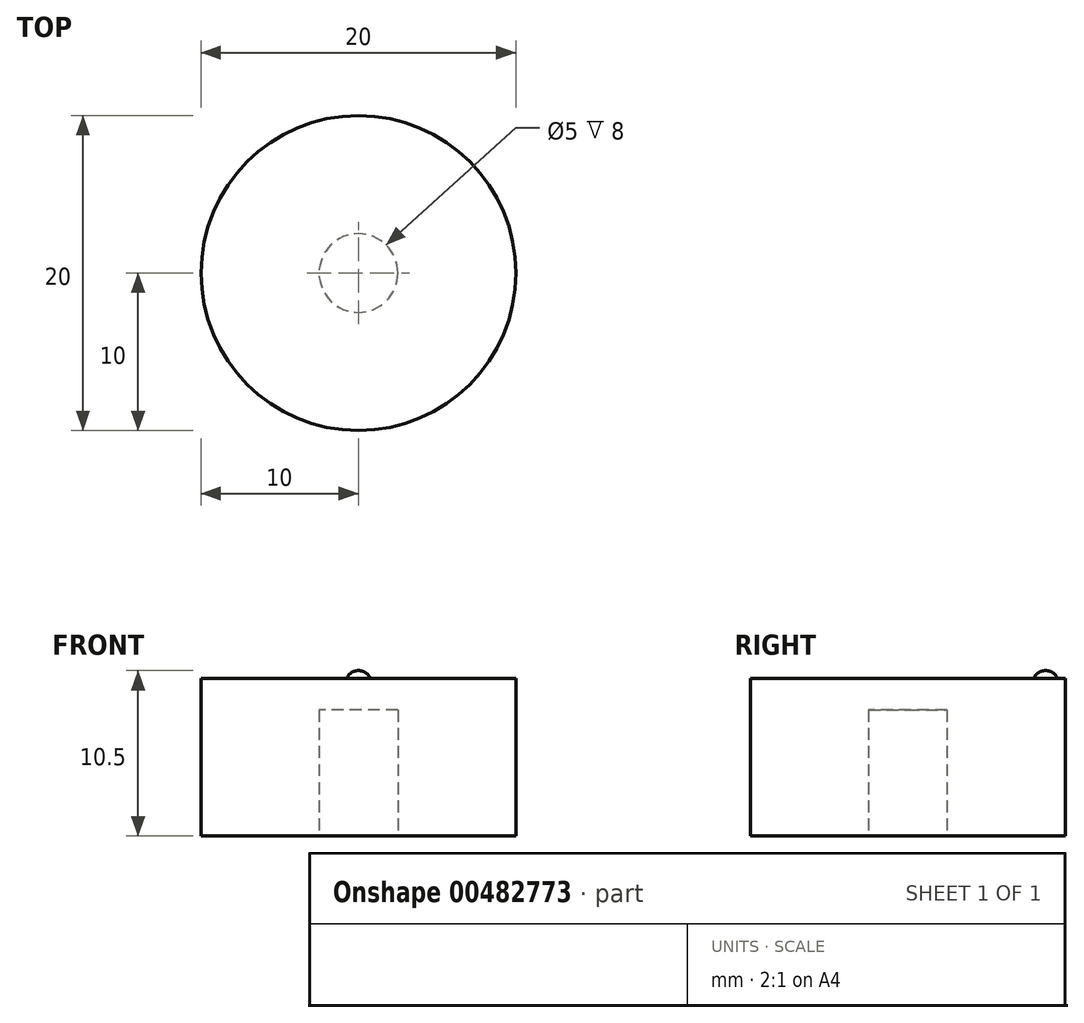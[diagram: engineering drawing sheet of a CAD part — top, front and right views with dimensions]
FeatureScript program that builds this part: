
annotation { "Feature Type Name" : "Feature", "Feature Type Description" : "" }
export const myFeature = defineFeature(function(context is Context, id is Id, definition is map)
    precondition{}
    {
        {
            var Q0;
            Q0=qCreatedBy(makeId("Top.planeOp"),FACE);
            var sketch = newSketch(context, id + "F0", { "sketchPlane" : qUnion([Q0])});
            skCircle(sketch, "E0", {"center": v(0, 0) * mm, "radius": 10 * mm});
            skCircle(sketch, "E1", {"center": v(0, 0) * mm, "radius": 2.5 * mm});
            skCircle(sketch, "E2", {"center": v(0, 8.75) * mm, "radius": 0.75 * mm});
            skSolve(sketch);
        }
        {
            var Q0;
            Q0=makeQuery(id+"F0.imprint","IMPRINT",FACE,{"disambiguationData":[TD([[makeQuery(id+"F0.imprint","IMPRINT",EDGE,{"derivedFrom":sQuery(id+"F0.wireOp",EDGE,"E0")}),1.0]])]});
            var Q1;
            Q1=makeQuery(id+"F0.imprint","IMPRINT",FACE,{"disambiguationData":[TD([[makeQuery(id+"F0.imprint","IMPRINT",EDGE,{"derivedFrom":sQuery(id+"F0.wireOp",EDGE,"E2")}),1.0]])]});
            var Q2;
            Q2=makeQuery(id+"F0.imprint","IMPRINT",FACE,{"disambiguationData":[TD([[makeQuery(id+"F0.imprint","IMPRINT",EDGE,{"derivedFrom":sQuery(id+"F0.wireOp",EDGE,"E1")}),1.0]])]});
            extrude(context, id + "F1", {"entities" : qUnion([Q0, Q1, Q2]), "depth" : 10 * mm});
        }
        {
            var Q0;
            Q0=makeQuery(id+"F0.imprint","IMPRINT",FACE,{"disambiguationData":[TD([[makeQuery(id+"F0.imprint","IMPRINT",EDGE,{"derivedFrom":sQuery(id+"F0.wireOp",EDGE,"E1")}),1.0]])]});
            extrude(context, id + "F2", {"entities" : qUnion([Q0]), "operationType" : NewBodyOperationType.REMOVE, "depth" : 8 * mm});
        }
        {
            var Q0;
            Q0=makeQuery(id+"F0.imprint","IMPRINT",FACE,{"disambiguationData":[TD([[makeQuery(id+"F0.imprint","IMPRINT",EDGE,{"derivedFrom":sQuery(id+"F0.wireOp",EDGE,"E2")}),1.0]])]});
            extrude(context, id + "F3", {"entities" : qUnion([Q0]), "operationType" : NewBodyOperationType.ADD, "depth" : 10.5 * mm});
        }
        {
            var Q0;
            Q0=makeQuery(id+"F3.opExtrude","CAP_EDGE",EDGE,{"disambiguationData":[OSD([sQuery(id+"F0.wireOp",EDGE,"E2")])],"isStart":false});
            fillet(context, id + "F4", {"entities" : qUnion([Q0]), "radius" : 0.8 * mm, "tangentPropagation" : true, "allowEdgeOverflow" : false});
        }
        {
            var Q0;
            Q0=makeQuery(id+"F4.opFillet","BLEND_EDGE",EDGE,{"blendedFrom":[makeQuery(id+"F3.opExtrude","CAP_EDGE",EDGE,{"disambiguationData":[OSD([sQuery(id+"F0.wireOp",EDGE,"E2")])],"isStart":false}),makeQuery(id+"F1.opExtrude","CAP_FACE",FACE,{"disambiguationData":[OSD([sQuery(id+"F0.wireOp",EDGE,"E0")])],"isStart":false})],"blendedInto":[makeQuery(id+"F1.opExtrude","CAP_FACE",FACE,{"disambiguationData":[OSD([sQuery(id+"F0.wireOp",EDGE,"E0")])],"isStart":false})]});
            fillet(context, id + "F5", {"entities" : qUnion([Q0]), "radius" : 0.2 * mm, "tangentPropagation" : true, "allowEdgeOverflow" : false});
        }
    });
